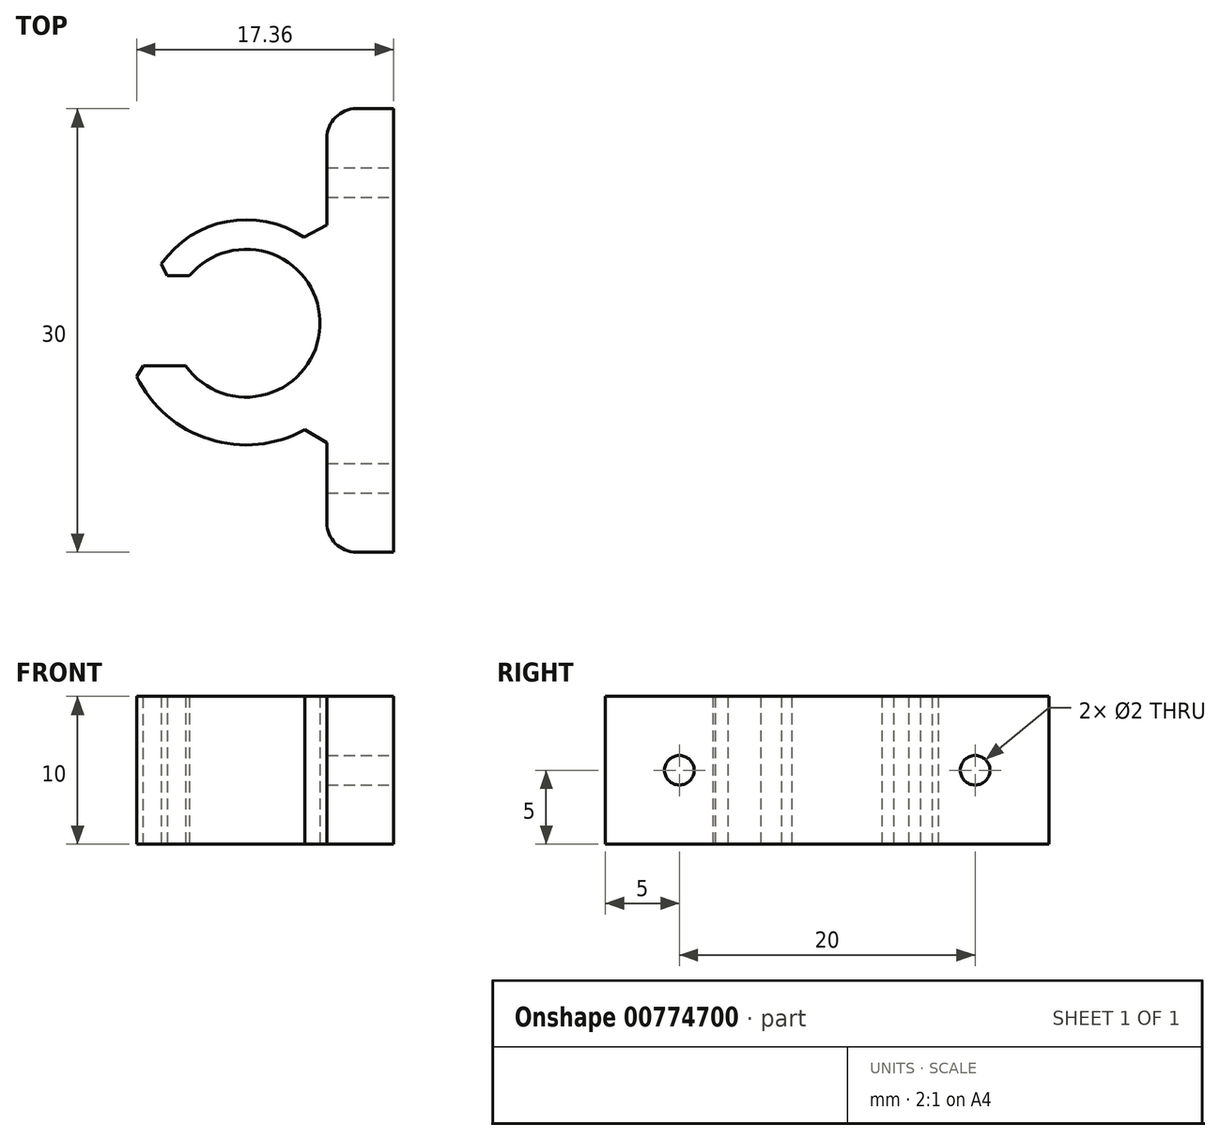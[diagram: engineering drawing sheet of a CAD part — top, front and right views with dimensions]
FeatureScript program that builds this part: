
annotation { "Feature Type Name" : "Feature", "Feature Type Description" : "" }
export const myFeature = defineFeature(function(context is Context, id is Id, definition is map)
    precondition{}
    {
        {
            var Q0;
            Q0=qCreatedBy(makeId("Top.planeOp"),FACE);
            var sketch = newSketch(context, id + "F0", { "sketchPlane" : qUnion([Q0])});
            skLineSegment(sketch, "E0.MirrorCS", {"start": v(14.88, 3.7) * mm, "end": v(12.49, 3.7) * mm});
            skLineSegment(sketch, "E1.MirrorCS", {"start": v(14.63, -2.4) * mm, "end": v(11, -2.4) * mm});
            skArc(sketch, "E2.MirrorCS", {"start": v(12.49, 3.7) * mm, "mid": v(18.01, 7.45) * mm, "end": v(24.17, 4.87) * mm});
            skArc(sketch, "E3.MirrorCS", {"start": v(24.17, -5.67) * mm, "mid": v(16.72, -7.5) * mm, "end": v(11, -2.4) * mm});
            skArc(sketch, "E4.MirrorCS", {"start": v(14.88, 3.7) * mm, "mid": v(23.7, 0.28) * mm, "end": v(14.63, -2.4) * mm});
            skCircle(sketch, "E5", {"center": v(18.67, 0.5) * mm, "radius": 5 * mm, "construction": true});
            skLineSegment(sketch, "E6.bottom", {"start": v(28.67, 15) * mm, "end": v(28.67, -15) * mm});
            skLineSegment(sketch, "E6.top", {"start": v(24.17, 15) * mm, "end": v(24.17, 4.87) * mm});
            skLineSegment(sketch, "E6.left", {"start": v(28.67, 15) * mm, "end": v(24.17, 15) * mm});
            skLineSegment(sketch, "E6.right", {"start": v(28.67, -15) * mm, "end": v(24.17, -15) * mm});
            skLineSegment(sketch, "E7.trimOffspring", {"start": v(24.17, -5.67) * mm, "end": v(24.17, -15) * mm});
            skSolve(sketch);
        }
        {
            var Q0;
            Q0 = qSketchRegion(id + "F0", true);
            extrude(context, id + "F1", {"entities" : qUnion([Q0]), "depth" : 10 * mm, "offsetDistance" : 25 * mm});
        }
        {
            var Q0;
            Q0=makeQuery(id+"F1.opExtrude","SWEPT_EDGE",EDGE,{"disambiguationData":[OSD([sQuery(id+"F0.wireOp",EDGE,"E2.MirrorCS"),sQuery(id+"F0.wireOp",EDGE,"E6.top")])]});
            var Q1;
            Q1=makeQuery(id+"F1.opExtrude","SWEPT_EDGE",EDGE,{"disambiguationData":[OSD([sQuery(id+"F0.wireOp",EDGE,"E3.MirrorCS"),sQuery(id+"F0.wireOp",EDGE,"E7.trimOffspring")])]});
            chamfer(context, id + "F2", {"entities" : qUnion([Q0, Q1]), "width" : 1 * mm, "tangentPropagation" : true});
        }
        {
            var Q0;
            Q0=makeQuery(id+"F1.opExtrude","SWEPT_EDGE",EDGE,{"disambiguationData":[OSD([sQuery(id+"F0.wireOp",EDGE,"E6.top"),sQuery(id+"F0.wireOp",EDGE,"E6.left")])]});
            var Q1;
            Q1=makeQuery(id+"F1.opExtrude","SWEPT_EDGE",EDGE,{"disambiguationData":[OSD([sQuery(id+"F0.wireOp",EDGE,"E6.right"),sQuery(id+"F0.wireOp",EDGE,"E7.trimOffspring")])]});
            fillet(context, id + "F3", {"entities" : qUnion([Q0, Q1]), "radius" : 2 * mm, "tangentPropagation" : true, "allowEdgeOverflow" : false});
        }
        {
            var Q0;
            Q0=makeQuery(id+"F1.opExtrude","SWEPT_EDGE",EDGE,{"disambiguationData":[OSD([sQuery(id+"F0.wireOp",EDGE,"E0.MirrorCS"),sQuery(id+"F0.wireOp",EDGE,"E2.MirrorCS")])]});
            var Q1;
            Q1=makeQuery(id+"F1.opExtrude","SWEPT_EDGE",EDGE,{"disambiguationData":[OSD([sQuery(id+"F0.wireOp",EDGE,"E1.MirrorCS"),sQuery(id+"F0.wireOp",EDGE,"E3.MirrorCS")])]});
            chamfer(context, id + "F4", {"entities" : qUnion([Q0, Q1]), "width" : 0.5 * mm, "tangentPropagation" : true});
        }
        {
            var Q0;
            Q0=makeQuery(id+"F1.opExtrude","SWEPT_FACE",FACE,{"disambiguationData":[OSD([sQuery(id+"F0.wireOp",EDGE,"E6.bottom")])]});
            var sketch = newSketch(context, id + "F5", { "sketchPlane" : qUnion([Q0])});
            skPoint(sketch, "E8", {"position": v(10, 5) * mm});
            skPoint(sketch, "E9.MirrorP", {"position": v(-10, 5) * mm});
            skSolve(sketch);
        }
        {
            var Q0;
            Q0=sQuery(id+"F5.wireOp",VERTEX,"E8");
            var Q1;
            Q1=sQuery(id+"F5.wireOp",VERTEX,"E9.MirrorP");
            var Q2;
            Q2=makeQuery(id+"F1.opExtrude","SWEPT_BODY",BODY,{"disambiguationData":[OSD([sQuery(id+"F0.wireOp",EDGE,"E0.MirrorCS"),sQuery(id+"F0.wireOp",EDGE,"E1.MirrorCS"),sQuery(id+"F0.wireOp",EDGE,"E2.MirrorCS"),sQuery(id+"F0.wireOp",EDGE,"E3.MirrorCS"),sQuery(id+"F0.wireOp",EDGE,"E4.MirrorCS"),sQuery(id+"F0.wireOp",EDGE,"E6.bottom"),sQuery(id+"F0.wireOp",EDGE,"E6.top"),sQuery(id+"F0.wireOp",EDGE,"E6.left"),sQuery(id+"F0.wireOp",EDGE,"E6.right"),sQuery(id+"F0.wireOp",EDGE,"E7.trimOffspring")])]});
            hole(context, id + "F6", {"style" : HoleStyle.SIMPLE, "endStyle" : HoleEndStyle.THROUGH, "holeDiameter" : 2 * mm, "majorDiameter" : 5 * mm, "isTappedThrough" : true, "tappedDepth" : 12 * mm, "tapClearance" : 3, "startFromSketch" : true, "locations" : qUnion([Q0, Q1]), "scope" : qUnion([Q2])});
        }
    });
